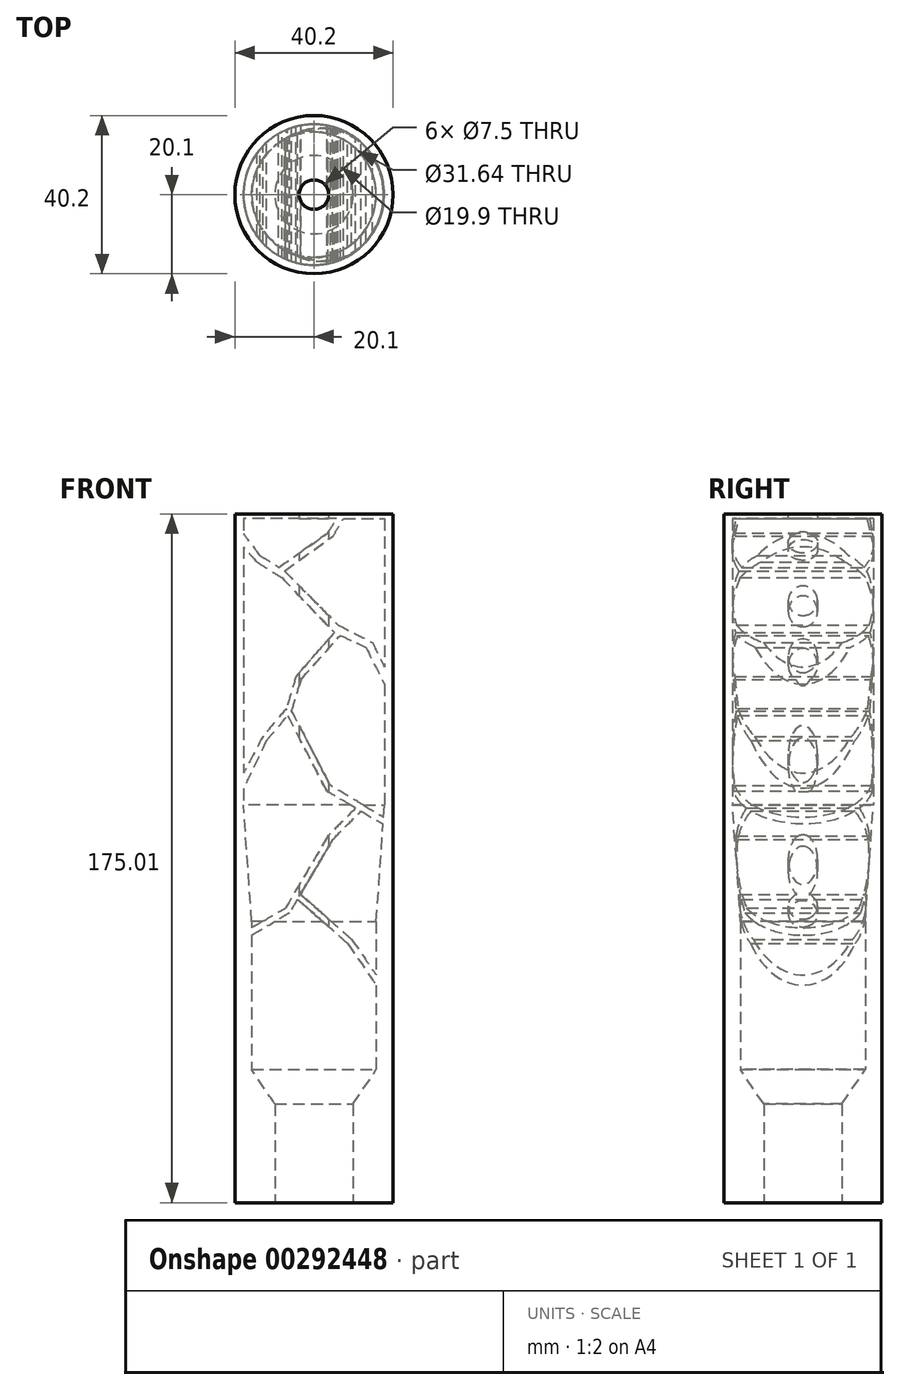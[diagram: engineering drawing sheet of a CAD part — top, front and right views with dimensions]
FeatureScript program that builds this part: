
annotation { "Feature Type Name" : "Feature", "Feature Type Description" : "" }
export const myFeature = defineFeature(function(context is Context, id is Id, definition is map)
    precondition{}
    {
        {
            var Q0;
            Q0=qCreatedBy(makeId("Front.planeOp"),FACE);
            var sketch = newSketch(context, id + "F0", { "sketchPlane" : qUnion([Q0])});
            skLineSegment(sketch, "E0", {"start": v(0, 0) * mm, "end": v(0, 175) * mm, "construction": true});
            skLineSegment(sketch, "E1", {"start": v(-3, 0) * mm, "end": v(-3, 175) * mm, "construction": true});
            skLineSegment(sketch, "E2", {"start": v(-3.5, -0.01) * mm, "end": v(-3.5, 175) * mm, "construction": true});
            skLineSegment(sketch, "E3", {"start": v(-9.9, 0) * mm, "end": v(-9.9, 175) * mm, "construction": true});
            skLineSegment(sketch, "E4", {"start": v(-20, 0) * mm, "end": v(-20, 175) * mm, "construction": true});
            skLineSegment(sketch, "E5", {"start": v(4.04, 175) * mm, "end": v(-22.22, 175) * mm, "construction": true});
            skLineSegment(sketch, "E6", {"start": v(23.08, 173.82) * mm, "end": v(-22.24, 173.82) * mm, "construction": true});
            skLineSegment(sketch, "E7", {"start": v(-17.94, 0) * mm, "end": v(-17.94, 175) * mm, "construction": true});
            skLineSegment(sketch, "E8", {"start": v(-22.12, 25) * mm, "end": v(22.75, 25) * mm, "construction": true});
            skLineSegment(sketch, "E9.MirrorCS", {"start": v(3, 0) * mm, "end": v(3, 175) * mm, "construction": true});
            skLineSegment(sketch, "E10.MirrorCS", {"start": v(17.94, 0) * mm, "end": v(17.94, 175) * mm, "construction": true});
            skLineSegment(sketch, "E11.MirrorCS", {"start": v(20, 0) * mm, "end": v(20, 175) * mm, "construction": true});
            skLineSegment(sketch, "E12.MirrorCS", {"start": v(9.9, 0) * mm, "end": v(9.9, 175) * mm, "construction": true});
            skLineSegment(sketch, "E13.MirrorCS", {"start": v(3.5, -0.01) * mm, "end": v(3.5, 175) * mm, "construction": true});
            skSolve(sketch);
        }
        {
            var Q0;
            Q0=qCreatedBy(makeId("Front.planeOp"),FACE);
            var sketch = newSketch(context, id + "F1", { "sketchPlane" : qUnion([Q0]), "disableImprinting" : false});
            skLineSegment(sketch, "E14", {"start": v(-18.18, 170.36) * mm, "end": v(-13.69, 164.42) * mm});
            skLineSegment(sketch, "E15", {"start": v(-7.52, 160.5) * mm, "end": v(6.1, 146.8) * mm});
            skLineSegment(sketch, "E16", {"start": v(6.1, 146.8) * mm, "end": v(14.83, 142.3) * mm});
            skLineSegment(sketch, "E17", {"start": v(14.83, 142.3) * mm, "end": v(18.14, 135.62) * mm});
            skLineSegment(sketch, "E18", {"start": v(-18.18, 166.91) * mm, "end": v(-14.47, 162.75) * mm});
            skLineSegment(sketch, "E19", {"start": v(-14.47, 162.75) * mm, "end": v(-8.16, 158.78) * mm});
            skLineSegment(sketch, "E20", {"start": v(-8.16, 158.78) * mm, "end": v(5.17, 144.84) * mm});
            skLineSegment(sketch, "E21", {"start": v(13.17, 141.1) * mm, "end": v(18.14, 131.23) * mm});
            skLineSegment(sketch, "E22", {"start": v(5.17, 144.84) * mm, "end": v(-4.56, 133.73) * mm});
            skLineSegment(sketch, "E23", {"start": v(-4.56, 133.73) * mm, "end": v(-7, 125.56) * mm});
            skLineSegment(sketch, "E24", {"start": v(-7, 125.56) * mm, "end": v(-13, 118.44) * mm});
            skLineSegment(sketch, "E25", {"start": v(-13, 118.44) * mm, "end": v(-18.1, 108.79) * mm});
            skLineSegment(sketch, "E26", {"start": v(6.7, 144.13) * mm, "end": v(-3.27, 132.97) * mm});
            skLineSegment(sketch, "E27", {"start": v(-3.27, 132.97) * mm, "end": v(-5.65, 124.9) * mm});
            skLineSegment(sketch, "E28", {"start": v(-12.05, 117.46) * mm, "end": v(-18.18, 104.65) * mm});
            skLineSegment(sketch, "E29", {"start": v(-5.65, 124.9) * mm, "end": v(4.16, 105.99) * mm});
            skLineSegment(sketch, "E30", {"start": v(4.16, 105.99) * mm, "end": v(18.19, 97.67) * mm});
            skLineSegment(sketch, "E31", {"start": v(-6.67, 123.72) * mm, "end": v(3.26, 104.57) * mm});
            skLineSegment(sketch, "E32", {"start": v(11.94, 99.46) * mm, "end": v(4.73, 92.25) * mm});
            skLineSegment(sketch, "E33", {"start": v(-6.2, 73.65) * mm, "end": v(-18.24, 66.54) * mm});
            skLineSegment(sketch, "E34", {"start": v(10.6, 100.25) * mm, "end": v(3.57, 93.2) * mm});
            skLineSegment(sketch, "E35", {"start": v(3.57, 93.2) * mm, "end": v(-7.24, 74.85) * mm});
            skLineSegment(sketch, "E36", {"start": v(-7.24, 74.85) * mm, "end": v(-18.28, 68.4) * mm});
            skLineSegment(sketch, "E37", {"start": v(-7.52, 160.5) * mm, "end": v(4.81, 169.32) * mm});
            skLineSegment(sketch, "E38", {"start": v(4.81, 169.32) * mm, "end": v(7.67, 174.04) * mm});
            skLineSegment(sketch, "E39", {"start": v(-8.95, 161.41) * mm, "end": v(3.46, 170.08) * mm});
            skLineSegment(sketch, "E40", {"start": v(3.46, 170.08) * mm, "end": v(5.98, 174.08) * mm});
            skLineSegment(sketch, "E41", {"start": v(-4.19, 77.08) * mm, "end": v(8.56, 65.84) * mm});
            skLineSegment(sketch, "E42", {"start": v(8.56, 65.84) * mm, "end": v(18.14, 51.86) * mm});
            skLineSegment(sketch, "E43", {"start": v(-3.44, 78.36) * mm, "end": v(9.57, 66.88) * mm});
            skLineSegment(sketch, "E44", {"start": v(9.57, 66.88) * mm, "end": v(18.14, 54.47) * mm});
            skLineSegment(sketch, "E45", {"start": v(-13.69, 164.42) * mm, "end": v(-8.95, 161.41) * mm});
            skLineSegment(sketch, "E46", {"start": v(-18.18, 170.36) * mm, "end": v(-18.18, 166.91) * mm});
            skLineSegment(sketch, "E47", {"start": v(13.17, 141.1) * mm, "end": v(6.7, 144.13) * mm});
            skLineSegment(sketch, "E48", {"start": v(18.14, 135.62) * mm, "end": v(18.14, 131.23) * mm});
            skLineSegment(sketch, "E49", {"start": v(-12.05, 117.46) * mm, "end": v(-6.67, 123.72) * mm});
            skLineSegment(sketch, "E50", {"start": v(18.19, 97.67) * mm, "end": v(18.19, 95.85) * mm});
            skLineSegment(sketch, "E51", {"start": v(18.19, 95.85) * mm, "end": v(11.94, 99.46) * mm});
            skLineSegment(sketch, "E52", {"start": v(10.6, 100.25) * mm, "end": v(3.26, 104.57) * mm});
            skLineSegment(sketch, "E53", {"start": v(4.73, 92.25) * mm, "end": v(-3.44, 78.36) * mm});
            skLineSegment(sketch, "E54", {"start": v(-4.19, 77.08) * mm, "end": v(-6.2, 73.65) * mm});
            skLineSegment(sketch, "E55", {"start": v(-18.28, 68.4) * mm, "end": v(-18.24, 66.54) * mm});
            skLineSegment(sketch, "E56", {"start": v(18.14, 54.47) * mm, "end": v(18.14, 51.86) * mm});
            skLineSegment(sketch, "E57", {"start": v(5.98, 174.08) * mm, "end": v(7.67, 174.04) * mm});
            skLineSegment(sketch, "E58", {"start": v(-18.1, 108.79) * mm, "end": v(-18.18, 104.65) * mm});
            skSolve(sketch);
        }
        {
            var Q0;
            Q0=qCreatedBy(makeId("Front.planeOp"),FACE);
            var sketch = newSketch(context, id + "F2", { "sketchPlane" : qUnion([Q0]), "disableImprinting" : false});
            skLineSegment(sketch, "E59", {"start": v(-20.1, 174.99) * mm, "end": v(-20.1, 0) * mm});
            skLineSegment(sketch, "E60", {"start": v(-20.1, 0) * mm, "end": v(-9.95, 0) * mm});
            skLineSegment(sketch, "E61", {"start": v(-9.95, 0) * mm, "end": v(-9.95, 25.06) * mm});
            skLineSegment(sketch, "E62", {"start": v(-17.9, 173.79) * mm, "end": v(-3.52, 173.79) * mm});
            skLineSegment(sketch, "E63", {"start": v(-3.52, 173.79) * mm, "end": v(-3.52, 175) * mm});
            skLineSegment(sketch, "E64", {"start": v(-3.52, 175) * mm, "end": v(-20.1, 174.99) * mm});
            skLineSegment(sketch, "E65", {"start": v(0, 0) * mm, "end": v(0, 25.6) * mm, "construction": true});
            skLineSegment(sketch, "E66", {"start": v(-17.9, 100.99) * mm, "end": v(-15.82, 71.42) * mm});
            skLineSegment(sketch, "E67", {"start": v(-15.82, 71.42) * mm, "end": v(-15.82, 33.82) * mm});
            skLineSegment(sketch, "E68", {"start": v(-17.9, 173.79) * mm, "end": v(-17.9, 100.99) * mm});
            skLineSegment(sketch, "E69", {"start": v(-15.82, 33.82) * mm, "end": v(-9.95, 25.06) * mm});
            skSolve(sketch);
        }
        {
            var Q0;
            Q0 = qSketchRegion(id + "F1", true);
            extrude(context, id + "F3", {"entities" : qUnion([Q0]), "depth" : 25 * mm, "hasSecondDirection" : true, "secondDirectionOppositeDirection" : true, "secondDirectionDepth" : 25 * mm});
        }
        {
            var Q0;
            Q0=qCreatedBy(makeId("Front.planeOp"),FACE);
            var sketch = newSketch(context, id + "F4", { "sketchPlane" : qUnion([Q0])});
            skLineSegment(sketch, "E70", {"start": v(17.93, 175.1) * mm, "end": v(17.93, -3.26) * mm});
            skLineSegment(sketch, "E71", {"start": v(17.93, -3.26) * mm, "end": v(50.8, -3.26) * mm});
            skLineSegment(sketch, "E72", {"start": v(50.8, -3.26) * mm, "end": v(50.8, 174.97) * mm});
            skLineSegment(sketch, "E73", {"start": v(50.8, 174.97) * mm, "end": v(17.93, 175.1) * mm});
            skSolve(sketch);
        }
        {
            var Q0;
            Q0 = qSketchRegion(id + "F4", true);
            var Q1;
            Q1=sQuery(id+"F0.wireOp",EDGE,"E0");
            revolve(context, id + "F5", {"operationType" : NewBodyOperationType.REMOVE, "entities" : qUnion([Q0]), "axis" : qUnion([Q1]), "revolveType" : RevolveType.FULL, "oppositeDirection" : true});
        }
        {
            var Q0;
            Q0 = qSketchRegion(id + "F2", true);
            var Q1;
            Q1=sQuery(id+"F2.wireOp",EDGE,"E65");
            revolve(context, id + "F6", {"operationType" : NewBodyOperationType.ADD, "entities" : qUnion([Q0]), "axis" : qUnion([Q1]), "revolveType" : RevolveType.FULL});
        }
        {
            var Q0;
            Q0=makeQuery(id+"F6.opRevolve","SWEPT_FACE",FACE,{"disambiguationData":[OSD([sQuery(id+"F2.wireOp",EDGE,"E60")])]});
            var sketch = newSketch(context, id + "F7", { "sketchPlane" : qUnion([Q0])});
            skCircle(sketch, "E74", {"center": v(0, 0) * mm, "radius": 3.75 * mm});
            skSolve(sketch);
        }
        {
            var Q0;
            Q0 = qSketchRegion(id + "F7", true);
            extrude(context, id + "F8", {"entities" : qUnion([Q0]), "operationType" : NewBodyOperationType.REMOVE, "endBound" : BoundingType.THROUGH_ALL, "oppositeDirection" : true, "depth" : 25 * mm});
        }
    });
